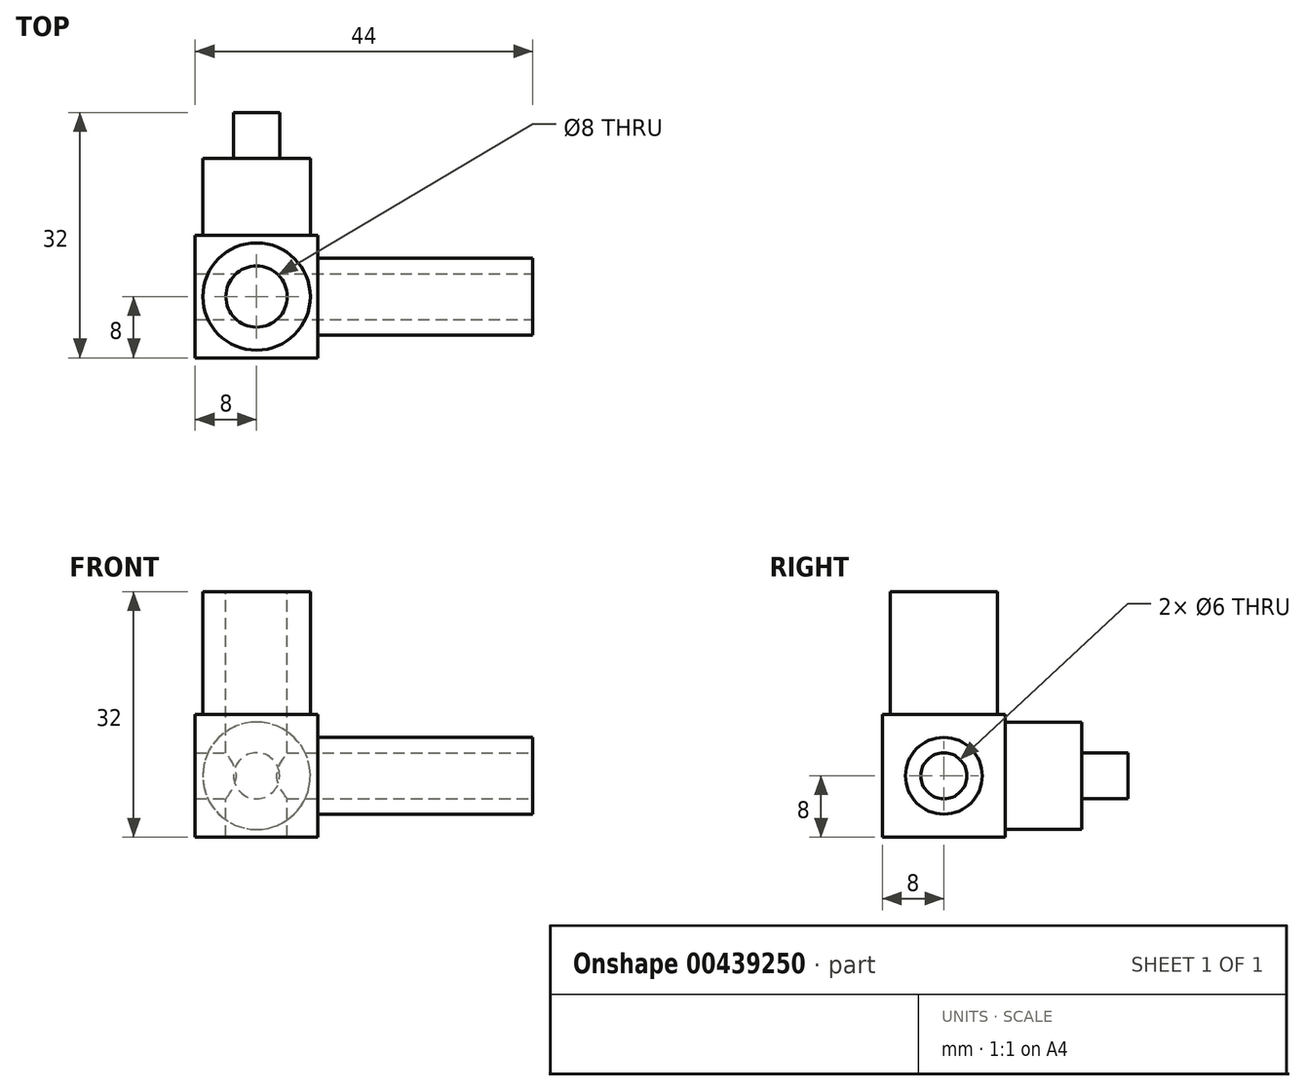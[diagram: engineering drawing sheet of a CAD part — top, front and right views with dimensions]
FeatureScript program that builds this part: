
annotation { "Feature Type Name" : "Feature", "Feature Type Description" : "" }
export const myFeature = defineFeature(function(context is Context, id is Id, definition is map)
    precondition{}
    {
        {
            var Q0;
            Q0=qCreatedBy(makeId("Top.planeOp"),FACE);
            var sketch = newSketch(context, id + "F0", { "sketchPlane" : qUnion([Q0])});
            skLineSegment(sketch, "E0.bottom", {"start": v(8, 8) * mm, "end": v(-8, 8) * mm});
            skLineSegment(sketch, "E0.top", {"start": v(8, -8) * mm, "end": v(-8, -8) * mm});
            skLineSegment(sketch, "E0.left", {"start": v(8, 8) * mm, "end": v(8, -8) * mm});
            skLineSegment(sketch, "E0.right", {"start": v(-8, 8) * mm, "end": v(-8, -8) * mm});
            skPoint(sketch, "E0.middle", {"position": v(0, 0) * mm});
            skSolve(sketch);
        }
        {
            var Q0;
            Q0=makeQuery(id+"F0.imprint","IMPRINT",FACE,{"disambiguationData":[TD([[makeQuery(id+"F0.imprint","IMPRINT",EDGE,{"derivedFrom":sQuery(id+"F0.wireOp",EDGE,"E0.bottom")}),1.0]])]});
            extrude(context, id + "F1", {"entities" : qUnion([Q0]), "depth" : 16 * mm});
        }
        {
            var Q0;
            Q0=makeQuery(id+"F1.opExtrude","SWEPT_FACE",FACE,{"disambiguationData":[OSD([sQuery(id+"F0.wireOp",EDGE,"E0.left")])]});
            var sketch = newSketch(context, id + "F2", { "sketchPlane" : qUnion([Q0])});
            skLineSegment(sketch, "E1", {"start": v(0, 0) * mm, "end": v(0, 24.37) * mm, "construction": true});
            skPoint(sketch, "E1.endSnap0", {"position": v(0, 16) * mm});
            skLineSegment(sketch, "E2", {"start": v(-16.85, 8) * mm, "end": v(20.42, 8) * mm, "construction": true});
            skCircle(sketch, "E3", {"center": v(0, 8) * mm, "radius": 5 * mm});
            skCircle(sketch, "E4", {"center": v(0, 8) * mm, "radius": 3 * mm});
            skSolve(sketch);
        }
        {
            var Q0;
            Q0=makeQuery(id+"F2.imprint","IMPRINT",FACE,{"disambiguationData":[TD([[makeQuery(id+"F2.imprint","IMPRINT",EDGE,{"derivedFrom":sQuery(id+"F2.wireOp",EDGE,"E4")}),1.0]])]});
            extrude(context, id + "F3", {"entities" : qUnion([Q0]), "operationType" : NewBodyOperationType.REMOVE, "oppositeDirection" : true, "depth" : 16 * mm});
        }
        {
            var Q0;
            Q0 = qSketchRegion(id + "F2", true);
            extrude(context, id + "F4", {"entities" : qUnion([Q0]), "operationType" : NewBodyOperationType.ADD, "depth" : 28 * mm});
        }
        {
            var Q0;
            Q0=makeQuery(id+"F1.opExtrude","CAP_FACE",FACE,{"disambiguationData":[OSD([sQuery(id+"F0.wireOp",EDGE,"E0.bottom"),sQuery(id+"F0.wireOp",EDGE,"E0.top"),sQuery(id+"F0.wireOp",EDGE,"E0.left"),sQuery(id+"F0.wireOp",EDGE,"E0.right")])],"isStart":false});
            var sketch = newSketch(context, id + "F5", { "sketchPlane" : qUnion([Q0])});
            skCircle(sketch, "E5", {"center": v(0, 0) * mm, "radius": 7 * mm});
            skCircle(sketch, "E6", {"center": v(0, 0) * mm, "radius": 4 * mm});
            skSolve(sketch);
        }
        {
            var Q0;
            Q0=makeQuery(id+"F5.imprint","IMPRINT",FACE,{"disambiguationData":[TD([[makeQuery(id+"F5.imprint","IMPRINT",EDGE,{"derivedFrom":sQuery(id+"F5.wireOp",EDGE,"E6")}),1.0]])]});
            extrude(context, id + "F6", {"entities" : qUnion([Q0]), "operationType" : NewBodyOperationType.REMOVE, "oppositeDirection" : true, "depth" : 16 * mm});
        }
        {
            var Q0;
            Q0 = qSketchRegion(id + "F5", true);
            extrude(context, id + "F7", {"entities" : qUnion([Q0]), "operationType" : NewBodyOperationType.ADD, "depth" : 16 * mm});
        }
        {
            var Q0;
            Q0=makeQuery(id+"F1.opExtrude","SWEPT_FACE",FACE,{"disambiguationData":[OSD([sQuery(id+"F0.wireOp",EDGE,"E0.bottom")])]});
            var sketch = newSketch(context, id + "F8", { "sketchPlane" : qUnion([Q0])});
            skLineSegment(sketch, "E7", {"start": v(-12.23, 8) * mm, "end": v(11.03, 8) * mm, "construction": true});
            skLineSegment(sketch, "E8", {"start": v(0, -5.03) * mm, "end": v(0, 20.2) * mm, "construction": true});
            skPoint(sketch, "E8.endSnap0", {"position": v(0, 16) * mm});
            skCircle(sketch, "E9", {"center": v(0, 8) * mm, "radius": 7 * mm});
            skCircle(sketch, "E10", {"center": v(0, 8) * mm, "radius": 3 * mm});
            skSolve(sketch);
        }
        {
            var Q0;
            Q0=makeQuery(id+"F8.imprint","IMPRINT",FACE,{"disambiguationData":[TD([[makeQuery(id+"F8.imprint","IMPRINT",EDGE,{"derivedFrom":sQuery(id+"F8.wireOp",EDGE,"E10")}),1.0]])]});
            extrude(context, id + "F9", {"entities" : qUnion([Q0]), "operationType" : NewBodyOperationType.ADD, "depth" : 16 * mm});
        }
        {
            var Q0;
            Q0 = qSketchRegion(id + "F8", true);
            extrude(context, id + "F10", {"entities" : qUnion([Q0]), "operationType" : NewBodyOperationType.ADD, "depth" : 10 * mm});
        }
    });
